# Revit family: Steel-HST Purlin-Steel & Tube-G500
name_source: partatom
category: Structural Framing
revit_build: Autodesk Revit 2018 (Build: 20170927_1515(x64)
units: mm (PartAtom-declared; Revit-internal decimal feet)

## family parameters
Always export as geometry = No
Always vertical = Yes
Cut with Voids When Loaded = No
Material for Model Behavior = Steel
OmniClass Number = 23.25.30.11.14.14
OmniClass Title = Beams
Section Shape = C Profile with Fold
Shared = No
Show family pre-cut in plan views = Yes
Structural Framing Length Roundoff = 0 mm

## types (9) — shared parameters
Assembly Code = B1020230
CBICode = 3411
CBIDescription = Structural steelwork
Coil Performance = Gauge 1.15-1.45mm; G500(MPa); 275g/m² (Zinc): Gauge 1.75-3.0mm; G450 (MPa); 275g/m²(Zinc)
Description = HST Steel Purlins and Girts are high strength lipped profile sections, providing an economic solution for your building project.
Design Instruction = All the design information should be cross referenced with the current Steel & Tube Purlins and Girts design guide, and AS/NZS 4600:2005
Design Standard = Steel & Tube’s HST purlins and Girts profiles are designed in accordance with AS/NZS 4600:2005.
Inner Fillet = 5.0 mm
Manufacturer = Steel & Tube
ManufacturerName = Steel & Tube
ManufacturerURL = http://www.steelandtube.co.nz
Material Standard = Steel & Tube’s HST purlins and Girts profiles are manufactured from materials conforming to AS1397:2011
ModifiedIssue_ANZRS = 20160330 $
Perimeter = 0.00 m²/m
Principal Axes Angle = 0.00°
Profile2 Height Validation = 152 mm  [stored 0.498688 ft]
SpecificationDescription = Steel & Tube Purlins & Girts
SpecificationReference = 3411ST
Structural Material = Metal-Steel-450MPa
Torsional Modulus = 0.0 mm³
Type Comments = HST Steel Purlins and Girts
URL = http://www.steelandtube.co.nz
Uniclass2015Code = Pr_20_76_51_21
Uniclass2015Title = Cold-formed galvanized steel sections
Uniclass2015Version = 2015
d1 = 59.0 mm

## per-type parameters (varying)
- HST100/12: Centroid Horizontal=16.8 mm; Centroid Vertical=51.0 mm; Elastic Modulus strong axis=8380.0 mm³; Elastic Modulus weak axis=2780.0 mm³; Fold Length=10.0 mm; Height=102.0 mm; Lip Length=15.0 mm; MassPerUnitLength_ANZRS=2.03 kg/m; Moment of Inertia strong axis=423000.00 mm4; Moment of Inertia weak axis=92000.00 mm4; Nominal Weight=2.03 kgf/m; Plastic Modulus strong axis=8380.0 mm³; Plastic Modulus weak axis=2780.0 mm³; Profile1=Yes; Profile2=No; Profile23Medium=No; Profile3=No; Profile3 Height Validation=203 mm  [stored 0.66601 ft]; Section Area=253.0 mm²; SectionAreaGross_ANZRS=253.0 mm²; SectionAreaNet_ANZRS=253.0 mm²; Shear Area strong axis=253.0 mm²; Shear Area weak axis=253.0 mm²; Torsional Moment of Inertia=111.00 mm4; Wall Design Thickness=1.2 mm; Wall Nominal Thickness=1.2 mm; Warping Constant=210000000.0 mm6; Width=51.0 mm; b1=8.0 mm; d2=10.0 mm; d3=25.0 mm; d4=48.0 mm
- HST100/15: Centroid Horizontal=16.6 mm; Centroid Vertical=51.0 mm; Elastic Modulus strong axis=10450.0 mm³; Elastic Modulus weak axis=3440.0 mm³; Fold Length=10.0 mm; Height=102.0 mm; Lip Length=15.0 mm; MassPerUnitLength_ANZRS=2.54 kg/m; Moment of Inertia strong axis=525000.00 mm4; Moment of Inertia weak axis=114000.00 mm4; Nominal Weight=2.54 kgf/m; Plastic Modulus strong axis=10450.0 mm³; Plastic Modulus weak axis=3440.0 mm³; Profile1=Yes; Profile2=No; Profile23Medium=No; Profile3=No; Profile3 Height Validation=203 mm  [stored 0.66601 ft]; Section Area=316.0 mm²; SectionAreaGross_ANZRS=316.0 mm²; SectionAreaNet_ANZRS=316.0 mm²; Shear Area strong axis=316.0 mm²; Shear Area weak axis=316.0 mm²; Torsional Moment of Inertia=222.00 mm4; Wall Design Thickness=1.5 mm; Wall Nominal Thickness=1.5 mm; Warping Constant=260000000.0 mm6; Width=51.0 mm; b1=8.0 mm; d2=10.0 mm; d3=25.0 mm; d4=48.0 mm
- HST150/12: Centroid Horizontal=23.5 mm; Centroid Vertical=76.0 mm; Elastic Modulus strong axis=18100.0 mm³; Elastic Modulus weak axis=6140.0 mm³; Fold Length=10.0 mm; Height=152.0 mm; Lip Length=24.0 mm; MassPerUnitLength_ANZRS=3.03 kg/m; Moment of Inertia strong axis=1380000.00 mm4; Moment of Inertia weak axis=249000.00 mm4; Nominal Weight=3.03 kgf/m; Plastic Modulus strong axis=18100.0 mm³; Plastic Modulus weak axis=6140.0 mm³; Profile1=No; Profile2=Yes; Profile23Medium=Yes; Profile3=No; Profile3 Height Validation=203 mm  [stored 0.66601 ft]; Section Area=386.0 mm²; SectionAreaGross_ANZRS=386.0 mm²; SectionAreaNet_ANZRS=386.0 mm²; Shear Area strong axis=386.0 mm²; Shear Area weak axis=386.0 mm²; Torsional Moment of Inertia=170.00 mm4; Wall Design Thickness=1.2 mm; Wall Nominal Thickness=1.2 mm; Warping Constant=1540000000.0 mm6; Width=65.0 mm; b1=8.0 mm; d2=10.0 mm; d3=7.0 mm; d4=48.0 mm
- HST150/15: Centroid Horizontal=23.2 mm; Centroid Vertical=76.0 mm; Elastic Modulus strong axis=22600.0 mm³; Elastic Modulus weak axis=7610.0 mm³; Fold Length=10.0 mm; Height=152.0 mm; Lip Length=24.0 mm; MassPerUnitLength_ANZRS=3.79 kg/m; Moment of Inertia strong axis=1720000.00 mm4; Moment of Inertia weak axis=308000.00 mm4; Nominal Weight=3.79 kgf/m; Plastic Modulus strong axis=22600.0 mm³; Plastic Modulus weak axis=7610.0 mm³; Profile1=No; Profile2=Yes; Profile23Medium=Yes; Profile3=No; Profile3 Height Validation=203 mm  [stored 0.66601 ft]; Section Area=483.0 mm²; SectionAreaGross_ANZRS=483.0 mm²; SectionAreaNet_ANZRS=483.0 mm²; Shear Area strong axis=483.0 mm²; Shear Area weak axis=483.0 mm²; Torsional Moment of Inertia=338.00 mm4; Wall Design Thickness=1.5 mm; Wall Nominal Thickness=1.5 mm; Warping Constant=1870000000.0 mm6; Width=65.0 mm; b1=8.0 mm; d2=10.0 mm; d3=7.0 mm; d4=48.0 mm
- HST200/12: Centroid Horizontal=25.1 mm; Centroid Vertical=101.5 mm; Elastic Modulus strong axis=29600.0 mm³; Elastic Modulus weak axis=8040.0 mm³; Fold Length=12.0 mm; Height=203.0 mm; Lip Length=25.0 mm; MassPerUnitLength_ANZRS=3.80 kg/m; Moment of Inertia strong axis=3000000.00 mm4; Moment of Inertia weak axis=392000.00 mm4; Nominal Weight=3.80 kgf/m; Plastic Modulus strong axis=29600.0 mm³; Plastic Modulus weak axis=8040.0 mm³; Profile1=No; Profile2=No; Profile23Medium=Yes; Profile3=Yes; Profile3 Height Validation=203 mm  [stored 0.66601 ft]; Section Area=478.0 mm²; SectionAreaGross_ANZRS=478.0 mm²; SectionAreaNet_ANZRS=478.0 mm²; Shear Area strong axis=478.0 mm²; Shear Area weak axis=478.0 mm²; Torsional Moment of Inertia=211.00 mm4; Wall Design Thickness=1.2 mm; Wall Nominal Thickness=1.2 mm; Warping Constant=3930000000.0 mm6; Width=75.0 mm; b1=8.0 mm; d2=10.0 mm; d3=10.0 mm; d4=48.0 mm
- HST200/15: Centroid Horizontal=24.9 mm; Centroid Vertical=101.5 mm; Elastic Modulus strong axis=36900.0 mm³; Elastic Modulus weak axis=9980.0 mm³; Fold Length=12.0 mm; Height=203.0 mm; Lip Length=25.0 mm; MassPerUnitLength_ANZRS=4.76 kg/m; Moment of Inertia strong axis=3750000.00 mm4; Moment of Inertia weak axis=486000.00 mm4; Nominal Weight=4.76 kgf/m; Plastic Modulus strong axis=36900.0 mm³; Plastic Modulus weak axis=9980.0 mm³; Profile1=No; Profile2=No; Profile23Medium=Yes; Profile3=Yes; Profile3 Height Validation=203 mm  [stored 0.66601 ft]; Section Area=598.0 mm²; SectionAreaGross_ANZRS=598.0 mm²; SectionAreaNet_ANZRS=598.0 mm²; Shear Area strong axis=598.0 mm²; Shear Area weak axis=598.0 mm²; Torsional Moment of Inertia=419.00 mm4; Wall Design Thickness=1.5 mm; Wall Nominal Thickness=1.5 mm; Warping Constant=4830000000.0 mm6; Width=75.0 mm; b1=8.0 mm; d2=10.0 mm; d3=10.0 mm; d4=48.0 mm
- HST250/13: Centroid Horizontal=28.7 mm; Centroid Vertical=125.0 mm; Elastic Modulus strong axis=46800.0 mm³; Elastic Modulus weak axis=11900.0 mm³; Fold Length=12.0 mm; Height=250.0 mm; Lip Length=33.0 mm; MassPerUnitLength_ANZRS=5.01 kg/m; Moment of Inertia strong axis=5850000.00 mm4; Moment of Inertia weak axis=655000.00 mm4; Nominal Weight=5.01 kgf/m; Plastic Modulus strong axis=46800.0 mm³; Plastic Modulus weak axis=11900.0 mm³; Profile1=No; Profile2=No; Profile23Medium=Yes; Profile3=Yes; Profile3 Height Validation=250 mm  [stored 0.82021 ft]; Section Area=625.0 mm²; SectionAreaGross_ANZRS=625.0 mm²; SectionAreaNet_ANZRS=625.0 mm²; Shear Area strong axis=625.0 mm²; Shear Area weak axis=625.0 mm²; Torsional Moment of Inertia=325.00 mm4; Wall Design Thickness=1.3 mm; Wall Nominal Thickness=1.3 mm; Warping Constant=10400000000.0 mm6; Width=85.0 mm; b1=10.0 mm; d2=14.0 mm; d3=25.0 mm; d4=73.0 mm
- HST250/15: Centroid Horizontal=28.6 mm; Centroid Vertical=125.0 mm; Elastic Modulus strong axis=54000.0 mm³; Elastic Modulus weak axis=13700.0 mm³; Fold Length=12.0 mm; Height=250.0 mm; Lip Length=33.0 mm; MassPerUnitLength_ANZRS=5.79 kg/m; Moment of Inertia strong axis=6760000.00 mm4; Moment of Inertia weak axis=753000.00 mm4; Nominal Weight=5.79 kgf/m; Plastic Modulus strong axis=54000.0 mm³; Plastic Modulus weak axis=13700.0 mm³; Profile1=No; Profile2=No; Profile23Medium=Yes; Profile3=Yes; Profile3 Height Validation=250 mm  [stored 0.82021 ft]; Section Area=722.0 mm²; SectionAreaGross_ANZRS=722.0 mm²; SectionAreaNet_ANZRS=722.0 mm²; Shear Area strong axis=722.0 mm²; Shear Area weak axis=722.0 mm²; Torsional Moment of Inertia=506.00 mm4; Wall Design Thickness=1.5 mm; Wall Nominal Thickness=1.5 mm; Warping Constant=11900000000.0 mm6; Width=85.0 mm; b1=10.0 mm; d2=14.0 mm; d3=25.0 mm; d4=73.0 mm
- HST300/15: Centroid Horizontal=32.1 mm; Centroid Vertical=150.0 mm; Elastic Modulus strong axis=76400.0 mm³; Elastic Modulus weak axis=18500.0 mm³; Fold Length=12.0 mm; Height=300.0 mm; Lip Length=38.0 mm; MassPerUnitLength_ANZRS=6.72 kg/m; Moment of Inertia strong axis=11500000.00 mm4; Moment of Inertia weak axis=1230000.00 mm4; Nominal Weight=6.72 kgf/m; Plastic Modulus strong axis=76400.0 mm³; Plastic Modulus weak axis=18500.0 mm³; Profile1=No; Profile2=No; Profile23Medium=Yes; Profile3=Yes; Profile3 Height Validation=300 mm; Section Area=847.0 mm²; SectionAreaGross_ANZRS=847.0 mm²; SectionAreaNet_ANZRS=847.0 mm²; Shear Area strong axis=847.0 mm²; Shear Area weak axis=847.0 mm²; Torsional Moment of Inertia=594.00 mm4; Wall Design Thickness=1.5 mm; Wall Nominal Thickness=1.5 mm; Warping Constant=26400000000.0 mm6; Width=100.0 mm; b1=10.0 mm; d2=64.0 mm; d3=25.0 mm; d4=123.0 mm

note: column(s) folded — value = type name in every type: Model

note: [stored X ft] marks values corroborated as IEEE doubles in the binary element streams (Revit-internal decimal feet)

## geometry (parser evidence)
native form markers: Sweep x6
no freeform markers — native parametric forms only
